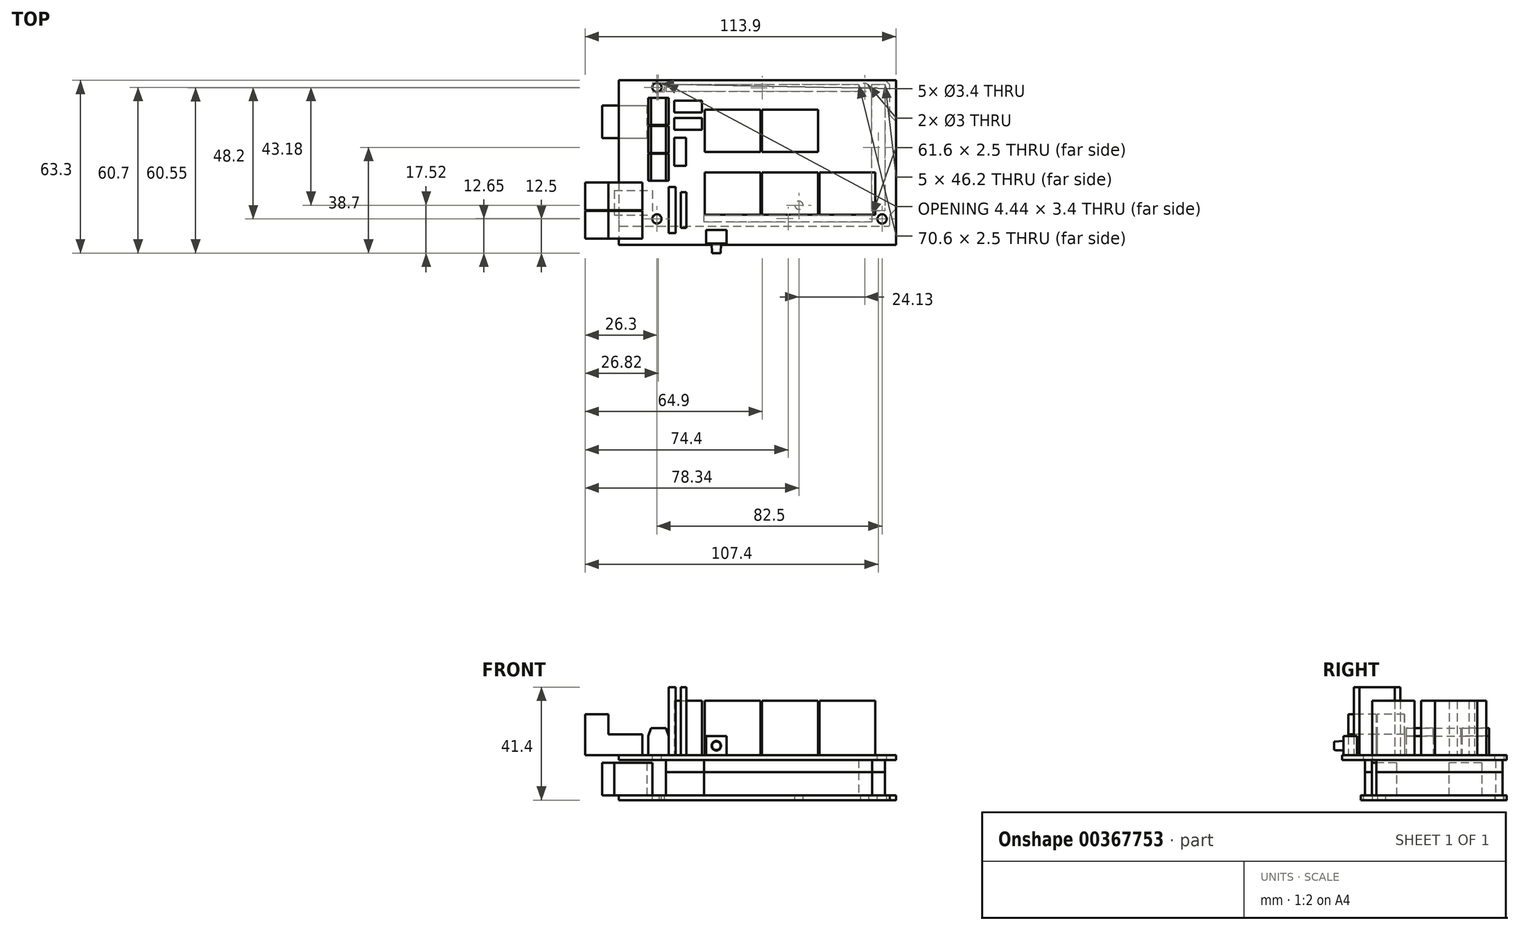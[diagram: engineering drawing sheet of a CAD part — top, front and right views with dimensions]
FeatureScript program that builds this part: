
annotation { "Feature Type Name" : "Feature", "Feature Type Description" : "" }
export const myFeature = defineFeature(function(context is Context, id is Id, definition is map)
    precondition{}
    {
        {
            var Q0;
            Q0=qCreatedBy(makeId("Top.planeOp"),FACE);
            var sketch = newSketch(context, id + "F0", { "sketchPlane" : qUnion([Q0])});
            skLineSegment(sketch, "E0.bottom", {"start": v(-50.8, 26.7) * mm, "end": v(50.8, 26.7) * mm, "construction": true});
            skLineSegment(sketch, "E0.top", {"start": v(-50.8, -26.7) * mm, "end": v(50.8, -26.7) * mm, "construction": true});
            skLineSegment(sketch, "E0.left", {"start": v(-50.8, 26.7) * mm, "end": v(-50.8, -26.7) * mm});
            skLineSegment(sketch, "E0.right", {"start": v(50.8, 26.7) * mm, "end": v(50.8, -26.7) * mm, "construction": true});
            skLineSegment(sketch, "E1", {"start": v(50.8, -26.7) * mm, "end": v(-50.8, 26.7) * mm, "construction": true});
            skLineSegment(sketch, "E2", {"start": v(-50.8, -26.7) * mm, "end": v(48.5, -26.7) * mm});
            skLineSegment(sketch, "E3", {"start": v(48.5, -26.7) * mm, "end": v(48.5, -22.7) * mm});
            skLineSegment(sketch, "E4", {"start": v(48.5, -22.7) * mm, "end": v(50.8, -20.4) * mm});
            skLineSegment(sketch, "E5", {"start": v(50.8, -20.4) * mm, "end": v(50.8, 11.6) * mm});
            skLineSegment(sketch, "E6", {"start": v(50.8, 11.6) * mm, "end": v(48.5, 13.9) * mm});
            skLineSegment(sketch, "E7", {"start": v(48.5, 13.9) * mm, "end": v(48.5, 25.1) * mm});
            skLineSegment(sketch, "E8", {"start": v(48.5, 25.1) * mm, "end": v(46.9, 26.7) * mm});
            skLineSegment(sketch, "E9", {"start": v(46.9, 26.7) * mm, "end": v(-50.8, 26.7) * mm});
            skSolve(sketch);
        }
        {
            var Q0;
            Q0=makeQuery(id+"F0.imprint","IMPRINT",FACE,{"disambiguationData":[TD([[makeQuery(id+"F0.imprint","IMPRINT",EDGE,{"derivedFrom":sQuery(id+"F0.wireOp",EDGE,"E0.left")}),1.0]])]});
            extrude(context, id + "F1", {"entities" : qUnion([Q0]), "depth" : 1.7 * mm});
        }
        {
            var Q0;
            Q0=makeQuery(id+"F1.opExtrude","CAP_FACE",FACE,{"disambiguationData":[OSD([sQuery(id+"F0.wireOp",EDGE,"E0.left"),sQuery(id+"F0.wireOp",EDGE,"E2"),sQuery(id+"F0.wireOp",EDGE,"E3"),sQuery(id+"F0.wireOp",EDGE,"E4"),sQuery(id+"F0.wireOp",EDGE,"E5"),sQuery(id+"F0.wireOp",EDGE,"E6"),sQuery(id+"F0.wireOp",EDGE,"E7"),sQuery(id+"F0.wireOp",EDGE,"E8"),sQuery(id+"F0.wireOp",EDGE,"E9")])],"isStart":false});
            var sketch = newSketch(context, id + "F2", { "sketchPlane" : qUnion([Q0])});
            skPoint(sketch, "E10", {"position": v(-35.56, 24.1) * mm});
            skPoint(sketch, "E11", {"position": v(39.37, 24.1) * mm});
            skPoint(sketch, "E12", {"position": v(15.24, -19.08) * mm});
            skPoint(sketch, "E13", {"position": v(-36.83, -24.16) * mm});
            skPoint(sketch, "E14", {"position": v(45.72, -24.16) * mm});
            skSolve(sketch);
        }
        {
            var Q0;
            Q0=sQuery(id+"F2.wireOp",VERTEX,"E10");
            var Q1;
            Q1=sQuery(id+"F2.wireOp",VERTEX,"E11");
            var Q2;
            Q2=sQuery(id+"F2.wireOp",VERTEX,"E12");
            var Q3;
            Q3=sQuery(id+"F2.wireOp",VERTEX,"E14");
            var Q4;
            Q4=sQuery(id+"F2.wireOp",VERTEX,"E13");
            var Q5;
            Q5=makeQuery(id+"F1.opExtrude","SWEPT_BODY",BODY,{"disambiguationData":[OSD([sQuery(id+"F0.wireOp",EDGE,"E0.left"),sQuery(id+"F0.wireOp",EDGE,"E2"),sQuery(id+"F0.wireOp",EDGE,"E3"),sQuery(id+"F0.wireOp",EDGE,"E4"),sQuery(id+"F0.wireOp",EDGE,"E5"),sQuery(id+"F0.wireOp",EDGE,"E6"),sQuery(id+"F0.wireOp",EDGE,"E7"),sQuery(id+"F0.wireOp",EDGE,"E8"),sQuery(id+"F0.wireOp",EDGE,"E9")])]});
            hole(context, id + "F3", {"style" : HoleStyle.SIMPLE, "endStyle" : HoleEndStyle.THROUGH, "holeDiameter" : 3 * mm, "locations" : qUnion([Q0, Q1, Q2, Q3, Q4]), "scope" : qUnion([Q5]), "isTappedThrough" : true});
        }
        {
            var Q0;
            Q0=makeQuery(id+"F1.opExtrude","SWEPT_EDGE",EDGE,{"disambiguationData":[OSD([sQuery(id+"F0.wireOp",EDGE,"E0.left"),sQuery(id+"F0.wireOp",EDGE,"E9")])]});
            var Q1;
            Q1=makeQuery(id+"F1.opExtrude","SWEPT_EDGE",EDGE,{"disambiguationData":[OSD([sQuery(id+"F0.wireOp",EDGE,"E0.left"),sQuery(id+"F0.wireOp",EDGE,"E2")])]});
            var Q2;
            Q2=makeQuery(id+"F1.opExtrude","SWEPT_EDGE",EDGE,{"disambiguationData":[OSD([sQuery(id+"F0.wireOp",EDGE,"E2"),sQuery(id+"F0.wireOp",EDGE,"E3")])]});
            var Q3;
            Q3=makeQuery(id+"F1.opExtrude","SWEPT_EDGE",EDGE,{"disambiguationData":[OSD([sQuery(id+"F0.wireOp",EDGE,"E3"),sQuery(id+"F0.wireOp",EDGE,"E4")])]});
            var Q4;
            Q4=makeQuery(id+"F1.opExtrude","SWEPT_EDGE",EDGE,{"disambiguationData":[OSD([sQuery(id+"F0.wireOp",EDGE,"E4"),sQuery(id+"F0.wireOp",EDGE,"E5")])]});
            var Q5;
            Q5=makeQuery(id+"F1.opExtrude","SWEPT_EDGE",EDGE,{"disambiguationData":[OSD([sQuery(id+"F0.wireOp",EDGE,"E5"),sQuery(id+"F0.wireOp",EDGE,"E6")])]});
            var Q6;
            Q6=makeQuery(id+"F1.opExtrude","SWEPT_EDGE",EDGE,{"disambiguationData":[OSD([sQuery(id+"F0.wireOp",EDGE,"E6"),sQuery(id+"F0.wireOp",EDGE,"E7")])]});
            var Q7;
            Q7=makeQuery(id+"F1.opExtrude","SWEPT_EDGE",EDGE,{"disambiguationData":[OSD([sQuery(id+"F0.wireOp",EDGE,"E7"),sQuery(id+"F0.wireOp",EDGE,"E8")])]});
            var Q8;
            Q8=makeQuery(id+"F1.opExtrude","SWEPT_EDGE",EDGE,{"disambiguationData":[OSD([sQuery(id+"F0.wireOp",EDGE,"E8"),sQuery(id+"F0.wireOp",EDGE,"E9")])]});
            fillet(context, id + "F4", {"entities" : qUnion([Q0, Q1, Q2, Q3, Q4, Q5, Q6, Q7, Q8]), "radius" : .5 * mm, "tangentPropagation" : true, "allowEdgeOverflow" : false});
        }
        {
            var Q0;
            Q0=makeQuery(id+"F1.opExtrude","CAP_FACE",FACE,{"disambiguationData":[OSD([sQuery(id+"F0.wireOp",EDGE,"E0.left"),sQuery(id+"F0.wireOp",EDGE,"E2"),sQuery(id+"F0.wireOp",EDGE,"E3"),sQuery(id+"F0.wireOp",EDGE,"E4"),sQuery(id+"F0.wireOp",EDGE,"E5"),sQuery(id+"F0.wireOp",EDGE,"E6"),sQuery(id+"F0.wireOp",EDGE,"E7"),sQuery(id+"F0.wireOp",EDGE,"E8"),sQuery(id+"F0.wireOp",EDGE,"E9")])],"isStart":false});
            var sketch = newSketch(context, id + "F5", { "sketchPlane" : qUnion([Q0])});
            skLineSegment(sketch, "E15.bottom", {"start": v(-52.4, -13.7) * mm, "end": v(-38.4, -13.7) * mm});
            skLineSegment(sketch, "E15.top", {"start": v(-52.4, -22.7) * mm, "end": v(-38.4, -22.7) * mm});
            skLineSegment(sketch, "E15.left", {"start": v(-52.4, -13.7) * mm, "end": v(-52.4, -22.7) * mm});
            skLineSegment(sketch, "E15.right", {"start": v(-38.4, -13.7) * mm, "end": v(-38.4, -22.7) * mm});
            skLineSegment(sketch, "E16.bottom", {"start": v(-56.9, 17.5) * mm, "end": v(-40.5, 17.5) * mm});
            skLineSegment(sketch, "E16.top", {"start": v(-56.9, 5.5) * mm, "end": v(-40.5, 5.5) * mm});
            skLineSegment(sketch, "E16.left", {"start": v(-56.9, 17.5) * mm, "end": v(-56.9, 5.5) * mm});
            skLineSegment(sketch, "E16.right", {"start": v(-40.5, 17.5) * mm, "end": v(-40.5, 5.5) * mm});
            skSolve(sketch);
        }
        {
            var Q0;
            {var subQ0=sQuery(id+"F5.wireOp",EDGE,"E16.left");Q0=makeQuery(id+"F5.imprint","IMPRINT",FACE,{"disambiguationData":[TD([[makeQuery(id+"F5.imprint","IMPRINT",EDGE,{"derivedFrom":subQ0}),1.0]])]});}
            var Q1;
            {var subQ0=sQuery(id+"F5.wireOp",EDGE,"E16.right");Q1=makeQuery(id+"F5.imprint","IMPRINT",FACE,{"disambiguationData":[TD([[makeQuery(id+"F5.imprint","IMPRINT",EDGE,{"derivedFrom":subQ0}),-1.0]])]});}
            var Q2;
            {var subQ0=sQuery(id+"F5.wireOp",EDGE,"E15.right");Q2=makeQuery(id+"F5.imprint","IMPRINT",FACE,{"disambiguationData":[TD([[makeQuery(id+"F5.imprint","IMPRINT",EDGE,{"derivedFrom":subQ0}),-1.0]])]});}
            var Q3;
            {var subQ0=sQuery(id+"F5.wireOp",EDGE,"E15.left");Q3=makeQuery(id+"F5.imprint","IMPRINT",FACE,{"disambiguationData":[TD([[makeQuery(id+"F5.imprint","IMPRINT",EDGE,{"derivedFrom":subQ0}),1.0]])]});}
            extrude(context, id + "F6", {"entities" : qUnion([Q0, Q1, Q2, Q3]), "depth" : 12 * mm});
        }
        {
            var Q0;
            Q0=makeQuery(id+"F1.opExtrude","CAP_FACE",FACE,{"disambiguationData":[OSD([sQuery(id+"F0.wireOp",EDGE,"E0.left"),sQuery(id+"F0.wireOp",EDGE,"E2"),sQuery(id+"F0.wireOp",EDGE,"E3"),sQuery(id+"F0.wireOp",EDGE,"E4"),sQuery(id+"F0.wireOp",EDGE,"E5"),sQuery(id+"F0.wireOp",EDGE,"E6"),sQuery(id+"F0.wireOp",EDGE,"E7"),sQuery(id+"F0.wireOp",EDGE,"E8"),sQuery(id+"F0.wireOp",EDGE,"E9")])],"isStart":false});
            var sketch = newSketch(context, id + "F7", { "sketchPlane" : qUnion([Q0])});
            skLineSegment(sketch, "E17.bottom", {"start": v(-33.5, 25.2) * mm, "end": v(37.1, 25.2) * mm});
            skLineSegment(sketch, "E17.top", {"start": v(-33.5, 22.7) * mm, "end": v(37.1, 22.7) * mm});
            skLineSegment(sketch, "E17.left", {"start": v(-33.5, 25.2) * mm, "end": v(-33.5, 22.7) * mm});
            skLineSegment(sketch, "E17.right", {"start": v(37.1, 25.2) * mm, "end": v(37.1, 22.7) * mm});
            skLineSegment(sketch, "E18.bottom", {"start": v(41.8, 25.2) * mm, "end": v(46.8, 25.2) * mm});
            skLineSegment(sketch, "E18.top", {"start": v(41.8, -21) * mm, "end": v(46.8, -21) * mm});
            skLineSegment(sketch, "E18.left", {"start": v(41.8, 25.2) * mm, "end": v(41.8, -21) * mm});
            skLineSegment(sketch, "E18.right", {"start": v(46.8, 25.2) * mm, "end": v(46.8, -21) * mm});
            skLineSegment(sketch, "E19.bottom", {"start": v(42.1, -25.2) * mm, "end": v(-19.5, -25.2) * mm});
            skLineSegment(sketch, "E19.top", {"start": v(42.1, -22.7) * mm, "end": v(-19.5, -22.7) * mm});
            skLineSegment(sketch, "E19.left", {"start": v(42.1, -25.2) * mm, "end": v(42.1, -22.7) * mm});
            skLineSegment(sketch, "E19.right", {"start": v(-19.5, -25.2) * mm, "end": v(-19.5, -22.7) * mm});
            skSolve(sketch);
        }
        {
            var Q0;
            Q0=qSketchRegion(id+"F7",true);
            extrude(context, id + "F8", {"entities" : qUnion([Q0]), "operationType" : NewBodyOperationType.ADD, "depth" : 8.6 * mm});
        }
        {
            var Q0;
            Q0=makeQuery(id+"F8.opExtrude","CAP_FACE",FACE,{"disambiguationData":[OSD([sQuery(id+"F7.wireOp",EDGE,"E17.bottom"),sQuery(id+"F7.wireOp",EDGE,"E17.top"),sQuery(id+"F7.wireOp",EDGE,"E17.left"),sQuery(id+"F7.wireOp",EDGE,"E17.right")])],"isStart":false});
            var sketch = newSketch(context, id + "F9", { "sketchPlane" : qUnion([Q0])});
            skLineSegment(sketch, "E20.1.0", {"start": v(41.8, 25.2) * mm, "end": v(41.8, -21) * mm});
            skLineSegment(sketch, "E20.1.1", {"start": v(41.8, -21) * mm, "end": v(46.8, -21) * mm});
            skLineSegment(sketch, "E20.1.2", {"start": v(46.8, -21) * mm, "end": v(46.8, 25.2) * mm});
            skLineSegment(sketch, "E20.1.3", {"start": v(46.8, 25.2) * mm, "end": v(41.8, 25.2) * mm});
            skLineSegment(sketch, "E20.2.0", {"start": v(42.1, -25.2) * mm, "end": v(42.1, -22.7) * mm});
            skLineSegment(sketch, "E20.2.1", {"start": v(42.1, -22.7) * mm, "end": v(-19.5, -22.7) * mm});
            skLineSegment(sketch, "E20.2.2", {"start": v(-19.5, -22.7) * mm, "end": v(-19.5, -25.2) * mm});
            skLineSegment(sketch, "E20.2.3", {"start": v(-19.5, -25.2) * mm, "end": v(42.1, -25.2) * mm});
            skLineSegment(sketch, "E21.0", {"start": v(-33.5, 22.7) * mm, "end": v(37.1, 22.7) * mm});
            skLineSegment(sketch, "E22.0", {"start": v(-33.5, 25.2) * mm, "end": v(-33.5, 22.7) * mm});
            skLineSegment(sketch, "E22.1", {"start": v(-33.5, 25.2) * mm, "end": v(37.1, 25.2) * mm});
            skLineSegment(sketch, "E22.2", {"start": v(37.1, 25.2) * mm, "end": v(37.1, 22.7) * mm});
            skSolve(sketch);
        }
        {
            var Q0;
            Q0=qSketchRegion(id+"F9",true);
            extrude(context, id + "F10", {"entities" : qUnion([Q0]), "depth" : 4.4 * mm});
        }
        {
            var Q0;
            Q0=makeQuery(id+"F10.opExtrude","CAP_FACE",FACE,{"disambiguationData":[OSD([sQuery(id+"F9.wireOp",EDGE,"E21.0"),sQuery(id+"F9.wireOp",EDGE,"E22.0"),sQuery(id+"F9.wireOp",EDGE,"E22.1"),sQuery(id+"F9.wireOp",EDGE,"E22.2")])],"isStart":false});
            var sketch = newSketch(context, id + "F11", { "sketchPlane" : qUnion([Q0])});
            skLineSegment(sketch, "E23", {"start": v(50.8, 26.7) * mm, "end": v(-50.8, 26.7) * mm});
            skLineSegment(sketch, "E24", {"start": v(-50.8, 26.7) * mm, "end": v(-50.8, -33.6) * mm});
            skLineSegment(sketch, "E25", {"start": v(-50.8, -33.6) * mm, "end": v(50.8, -33.6) * mm});
            skLineSegment(sketch, "E26", {"start": v(50.8, -33.6) * mm, "end": v(50.8, 26.7) * mm});
            skSolve(sketch);
        }
        {
            var Q0;
            Q0=qSketchRegion(id+"F11",true);
            extrude(context, id + "F12", {"entities" : qUnion([Q0]), "operationType" : NewBodyOperationType.ADD, "depth" : 1.7 * mm});
        }
        {
            var Q0;
            Q0=makeQuery(id+"F12.opExtrude","CAP_FACE",FACE,{"disambiguationData":[OSD([sQuery(id+"F11.wireOp",EDGE,"E23"),sQuery(id+"F11.wireOp",EDGE,"E24"),sQuery(id+"F11.wireOp",EDGE,"E25"),sQuery(id+"F11.wireOp",EDGE,"E26")])],"isStart":false});
            var sketch = newSketch(context, id + "F13", { "sketchPlane" : qUnion([Q0])});
            skPoint(sketch, "E27", {"position": v(-36.8, 24.1) * mm});
            skPoint(sketch, "E28", {"position": v(-36.8, -24.1) * mm});
            skPoint(sketch, "E29", {"position": v(45.7, -24.1) * mm});
            skSolve(sketch);
        }
        {
            var Q0;
            Q0=sQuery(id+"F13.wireOp",VERTEX,"E28");
            var Q1;
            Q1=sQuery(id+"F13.wireOp",VERTEX,"E27");
            var Q2;
            Q2=sQuery(id+"F13.wireOp",VERTEX,"E29");
            var Q3;
            Q3=makeQuery(id+"F1.opExtrude","SWEPT_BODY",BODY,{"disambiguationData":[OSD([sQuery(id+"F0.wireOp",EDGE,"E0.left"),sQuery(id+"F0.wireOp",EDGE,"E2"),sQuery(id+"F0.wireOp",EDGE,"E3"),sQuery(id+"F0.wireOp",EDGE,"E4"),sQuery(id+"F0.wireOp",EDGE,"E5"),sQuery(id+"F0.wireOp",EDGE,"E6"),sQuery(id+"F0.wireOp",EDGE,"E7"),sQuery(id+"F0.wireOp",EDGE,"E8"),sQuery(id+"F0.wireOp",EDGE,"E9")])]});
            var Q4;
            Q4=makeQuery(id+"F10.opExtrude","SWEPT_BODY",BODY,{"disambiguationData":[OSD([sQuery(id+"F9.wireOp",EDGE,"E20.1.0"),sQuery(id+"F9.wireOp",EDGE,"E20.1.1"),sQuery(id+"F9.wireOp",EDGE,"E20.1.2"),sQuery(id+"F9.wireOp",EDGE,"E20.1.3")])]});
            hole(context, id + "F14", {"style" : HoleStyle.SIMPLE, "endStyle" : HoleEndStyle.THROUGH, "holeDiameter" : 3.4 * mm, "locations" : qUnion([Q0, Q1, Q2]), "scope" : qUnion([Q3, Q4]), "isTappedThrough" : true});
        }
        {
            var Q0;
            Q0=makeQuery(id+"F12.opExtrude","CAP_FACE",FACE,{"disambiguationData":[OSD([sQuery(id+"F11.wireOp",EDGE,"E23"),sQuery(id+"F11.wireOp",EDGE,"E24"),sQuery(id+"F11.wireOp",EDGE,"E25"),sQuery(id+"F11.wireOp",EDGE,"E26")])],"isStart":false});
            var sketch = newSketch(context, id + "F15", { "sketchPlane" : qUnion([Q0])});
            skLineSegment(sketch, "E30.bottom", {"start": v(-42.1, -21.15) * mm, "end": v(-63.1, -21.15) * mm});
            skLineSegment(sketch, "E30.top", {"start": v(-42.1, -31.3) * mm, "end": v(-63.1, -31.3) * mm});
            skLineSegment(sketch, "E30.left", {"start": v(-42.1, -21.15) * mm, "end": v(-42.1, -31.3) * mm});
            skLineSegment(sketch, "E30.right", {"start": v(-63.1, -21.15) * mm, "end": v(-63.1, -31.3) * mm});
            skLineSegment(sketch, "E31.bottom", {"start": v(-42.1, -10.7) * mm, "end": v(-63.1, -10.7) * mm});
            skLineSegment(sketch, "E31.top", {"start": v(-42.1, -20.85) * mm, "end": v(-63.1, -20.85) * mm});
            skLineSegment(sketch, "E31.left", {"start": v(-42.1, -10.7) * mm, "end": v(-42.1, -20.85) * mm});
            skLineSegment(sketch, "E31.right", {"start": v(-63.1, -10.7) * mm, "end": v(-63.1, -20.85) * mm});
            skSolve(sketch);
        }
        {
            var Q0;
            Q0=qSketchRegion(id+"F15",true);
            extrude(context, id + "F16", {"entities" : qUnion([Q0]), "depth" : 15 * mm});
        }
        {
            var Q0;
            Q0=makeQuery(id+"F16.opExtrude","SWEPT_FACE",FACE,{"disambiguationData":[OSD([sQuery(id+"F15.wireOp",EDGE,"E30.top")])]});
            var sketch = newSketch(context, id + "F17", { "sketchPlane" : qUnion([Q0])});
            skLineSegment(sketch, "E32.bottom", {"start": v(-54.6, 31.4) * mm, "end": v(-42.1, 31.4) * mm});
            skLineSegment(sketch, "E32.top", {"start": v(-54.6, 24.1) * mm, "end": v(-42.1, 24.1) * mm});
            skLineSegment(sketch, "E32.left", {"start": v(-54.6, 31.4) * mm, "end": v(-54.6, 24.1) * mm});
            skLineSegment(sketch, "E32.right", {"start": v(-42.1, 31.4) * mm, "end": v(-42.1, 24.1) * mm});
            skSolve(sketch);
        }
        {
            var Q0;
            Q0=qSketchRegion(id+"F17",true);
            var Q1;
            Q1=makeQuery(id+"F16.opExtrude","SWEPT_FACE",FACE,{"disambiguationData":[OSD([sQuery(id+"F15.wireOp",EDGE,"E31.bottom")])]});
            extrude(context, id + "F18", {"entities" : qUnion([Q0]), "operationType" : NewBodyOperationType.REMOVE, "endBound" : BoundingType.UP_TO_SURFACE, "oppositeDirection" : true, "endBoundEntityFace" : qUnion([Q1]), "depth" : 25 * mm});
        }
        {
            var Q0;
            Q0=makeQuery(id+"F12.opExtrude","CAP_FACE",FACE,{"disambiguationData":[OSD([sQuery(id+"F11.wireOp",EDGE,"E23"),sQuery(id+"F11.wireOp",EDGE,"E24"),sQuery(id+"F11.wireOp",EDGE,"E25"),sQuery(id+"F11.wireOp",EDGE,"E26")])],"isStart":false});
            var sketch = newSketch(context, id + "F19", { "sketchPlane" : qUnion([Q0])});
            skLineSegment(sketch, "E33.bottom", {"start": v(-40, 20.2) * mm, "end": v(-32.5, 20.2) * mm});
            skLineSegment(sketch, "E33.top", {"start": v(-40, 10.3) * mm, "end": v(-32.5, 10.3) * mm});
            skLineSegment(sketch, "E33.left", {"start": v(-40, 20.2) * mm, "end": v(-40, 10.3) * mm});
            skLineSegment(sketch, "E33.right", {"start": v(-32.5, 20.2) * mm, "end": v(-32.5, 10.3) * mm});
            skLineSegment(sketch, "E34.bottom", {"start": v(-40, 10) * mm, "end": v(-32.5, 10) * mm});
            skLineSegment(sketch, "E34.top", {"start": v(-40, 0.1) * mm, "end": v(-32.5, 0.1) * mm});
            skLineSegment(sketch, "E34.left", {"start": v(-40, 10) * mm, "end": v(-40, 0.1) * mm});
            skLineSegment(sketch, "E34.right", {"start": v(-32.5, 10) * mm, "end": v(-32.5, 0.1) * mm});
            skLineSegment(sketch, "E35.bottom", {"start": v(-40, -0.2) * mm, "end": v(-32.5, -0.2) * mm});
            skLineSegment(sketch, "E35.top", {"start": v(-40, -10.1) * mm, "end": v(-32.5, -10.1) * mm});
            skLineSegment(sketch, "E35.left", {"start": v(-40, -0.2) * mm, "end": v(-40, -10.1) * mm});
            skLineSegment(sketch, "E35.right", {"start": v(-32.5, -0.2) * mm, "end": v(-32.5, -10.1) * mm});
            skSolve(sketch);
        }
        {
            var Q0;
            Q0=qSketchRegion(id+"F19",true);
            extrude(context, id + "F20", {"entities" : qUnion([Q0]), "depth" : 10 * mm});
        }
        {
            var Q0;
            Q0=makeQuery(id+"F20.opExtrude","CAP_EDGE",EDGE,{"disambiguationData":[OSD([sQuery(id+"F19.wireOp",EDGE,"E33.left")])],"isStart":false});
            var Q1;
            Q1=makeQuery(id+"F20.opExtrude","CAP_EDGE",EDGE,{"disambiguationData":[OSD([sQuery(id+"F19.wireOp",EDGE,"E34.left")])],"isStart":false});
            var Q2;
            Q2=makeQuery(id+"F20.opExtrude","CAP_EDGE",EDGE,{"disambiguationData":[OSD([sQuery(id+"F19.wireOp",EDGE,"E35.left")])],"isStart":false});
            var Q3;
            Q3=makeQuery(id+"F20.opExtrude","CAP_EDGE",EDGE,{"disambiguationData":[OSD([sQuery(id+"F19.wireOp",EDGE,"E35.right")])],"isStart":false});
            var Q4;
            Q4=makeQuery(id+"F20.opExtrude","CAP_EDGE",EDGE,{"disambiguationData":[OSD([sQuery(id+"F19.wireOp",EDGE,"E34.right")])],"isStart":false});
            var Q5;
            Q5=makeQuery(id+"F20.opExtrude","CAP_EDGE",EDGE,{"disambiguationData":[OSD([sQuery(id+"F19.wireOp",EDGE,"E33.right")])],"isStart":false});
            chamfer(context, id + "F21", {"entities" : qUnion([Q0, Q1, Q2, Q3, Q4, Q5]), "chamferType" : ChamferType.TWO_OFFSETS, "width1" : 1 * mm, "oppositeDirection" : false, "width2" : 3 * mm, "tangentPropagation" : true});
        }
        {
            var Q0;
            Q0=makeQuery(id+"F12.opExtrude","CAP_FACE",FACE,{"disambiguationData":[OSD([sQuery(id+"F11.wireOp",EDGE,"E23"),sQuery(id+"F11.wireOp",EDGE,"E24"),sQuery(id+"F11.wireOp",EDGE,"E25"),sQuery(id+"F11.wireOp",EDGE,"E26")])],"isStart":false});
            var sketch = newSketch(context, id + "F22", { "sketchPlane" : qUnion([Q0])});
            skLineSegment(sketch, "E36.bottom", {"start": v(-30.5, 19.2) * mm, "end": v(-20.3, 19.2) * mm});
            skLineSegment(sketch, "E36.top", {"start": v(-30.5, 14.9) * mm, "end": v(-20.3, 14.9) * mm});
            skLineSegment(sketch, "E36.left", {"start": v(-30.5, 19.2) * mm, "end": v(-30.5, 14.9) * mm});
            skLineSegment(sketch, "E36.right", {"start": v(-20.3, 19.2) * mm, "end": v(-20.3, 14.9) * mm});
            skLineSegment(sketch, "E37.bottom", {"start": v(-30.5, 12.9) * mm, "end": v(-20.3, 12.9) * mm});
            skLineSegment(sketch, "E37.top", {"start": v(-30.5, 8.6) * mm, "end": v(-20.3, 8.6) * mm});
            skLineSegment(sketch, "E37.left", {"start": v(-30.5, 12.9) * mm, "end": v(-30.5, 8.6) * mm});
            skLineSegment(sketch, "E37.right", {"start": v(-20.3, 12.9) * mm, "end": v(-20.3, 8.6) * mm});
            skLineSegment(sketch, "E38.bottom", {"start": v(-30.5, 5.6) * mm, "end": v(-26.2, 5.6) * mm});
            skLineSegment(sketch, "E38.top", {"start": v(-30.5, -4.6) * mm, "end": v(-26.2, -4.6) * mm});
            skLineSegment(sketch, "E38.left", {"start": v(-30.5, 5.6) * mm, "end": v(-30.5, -4.6) * mm});
            skLineSegment(sketch, "E38.right", {"start": v(-26.2, 5.6) * mm, "end": v(-26.2, -4.6) * mm});
            skLineSegment(sketch, "E39.bottom", {"start": v(-19.3, 15.9) * mm, "end": v(1.2, 15.9) * mm});
            skLineSegment(sketch, "E39.top", {"start": v(-19.3, 0.4) * mm, "end": v(1.2, 0.4) * mm});
            skLineSegment(sketch, "E39.left", {"start": v(-19.3, 15.9) * mm, "end": v(-19.3, 0.4) * mm});
            skLineSegment(sketch, "E39.right", {"start": v(1.2, 15.9) * mm, "end": v(1.2, 0.4) * mm});
            skLineSegment(sketch, "E40.bottom", {"start": v(1.7, 15.9) * mm, "end": v(22.2, 15.9) * mm});
            skLineSegment(sketch, "E40.top", {"start": v(1.7, 0.4) * mm, "end": v(22.2, 0.4) * mm});
            skLineSegment(sketch, "E40.left", {"start": v(1.7, 15.9) * mm, "end": v(1.7, 0.4) * mm});
            skLineSegment(sketch, "E40.right", {"start": v(22.2, 15.9) * mm, "end": v(22.2, 0.4) * mm});
            skLineSegment(sketch, "E41.bottom", {"start": v(-19.3, -7.1) * mm, "end": v(1.2, -7.1) * mm});
            skLineSegment(sketch, "E41.top", {"start": v(-19.3, -22.6) * mm, "end": v(1.2, -22.6) * mm});
            skLineSegment(sketch, "E41.left", {"start": v(-19.3, -7.1) * mm, "end": v(-19.3, -22.6) * mm});
            skLineSegment(sketch, "E41.right", {"start": v(1.2, -7.1) * mm, "end": v(1.2, -22.6) * mm});
            skLineSegment(sketch, "E42.bottom", {"start": v(1.7, -7.1) * mm, "end": v(22.2, -7.1) * mm});
            skLineSegment(sketch, "E42.top", {"start": v(1.7, -22.6) * mm, "end": v(22.2, -22.6) * mm});
            skLineSegment(sketch, "E42.left", {"start": v(1.7, -7.1) * mm, "end": v(1.7, -22.6) * mm});
            skLineSegment(sketch, "E42.right", {"start": v(22.2, -7.1) * mm, "end": v(22.2, -22.6) * mm});
            skLineSegment(sketch, "E43.bottom", {"start": v(22.7, -7.1) * mm, "end": v(43.2, -7.1) * mm});
            skLineSegment(sketch, "E43.top", {"start": v(22.7, -22.6) * mm, "end": v(43.2, -22.6) * mm});
            skLineSegment(sketch, "E43.left", {"start": v(22.7, -7.1) * mm, "end": v(22.7, -22.6) * mm});
            skLineSegment(sketch, "E43.right", {"start": v(43.2, -7.1) * mm, "end": v(43.2, -22.6) * mm});
            skSolve(sketch);
        }
        {
            var Q0;
            Q0=qSketchRegion(id+"F22",true);
            extrude(context, id + "F23", {"entities" : qUnion([Q0]), "operationType" : NewBodyOperationType.ADD, "depth" : 20 * mm});
        }
        {
            var Q0;
            Q0=makeQuery(id+"F12.opExtrude","CAP_FACE",FACE,{"disambiguationData":[OSD([sQuery(id+"F11.wireOp",EDGE,"E23"),sQuery(id+"F11.wireOp",EDGE,"E24"),sQuery(id+"F11.wireOp",EDGE,"E25"),sQuery(id+"F11.wireOp",EDGE,"E26")])],"isStart":false});
            var sketch = newSketch(context, id + "F24", { "sketchPlane" : qUnion([Q0])});
            skLineSegment(sketch, "E44.bottom", {"start": v(-32.5, -12.33) * mm, "end": v(-30, -12.33) * mm});
            skLineSegment(sketch, "E44.top", {"start": v(-32.5, -29.33) * mm, "end": v(-30, -29.33) * mm});
            skLineSegment(sketch, "E44.left", {"start": v(-32.5, -12.33) * mm, "end": v(-32.5, -29.33) * mm});
            skLineSegment(sketch, "E44.right", {"start": v(-30, -12.33) * mm, "end": v(-30, -29.33) * mm});
            skLineSegment(sketch, "E45.bottom", {"start": v(-28, -14.33) * mm, "end": v(-26, -14.33) * mm});
            skLineSegment(sketch, "E45.top", {"start": v(-28, -27.33) * mm, "end": v(-26, -27.33) * mm});
            skLineSegment(sketch, "E45.left", {"start": v(-28, -14.33) * mm, "end": v(-28, -27.33) * mm});
            skLineSegment(sketch, "E45.right", {"start": v(-26, -14.33) * mm, "end": v(-26, -27.33) * mm});
            skLineSegment(sketch, "E46", {"start": v(-30, -20.83) * mm, "end": v(-28, -20.83) * mm});
            skSolve(sketch);
        }
        {
            var Q0;
            Q0=qSketchRegion(id+"F24",true);
            extrude(context, id + "F25", {"entities" : qUnion([Q0]), "depth" : 25 * mm});
        }
        {
            var Q0;
            Q0=makeQuery(id+"F12.opExtrude","CAP_FACE",FACE,{"disambiguationData":[OSD([sQuery(id+"F11.wireOp",EDGE,"E23"),sQuery(id+"F11.wireOp",EDGE,"E24"),sQuery(id+"F11.wireOp",EDGE,"E25"),sQuery(id+"F11.wireOp",EDGE,"E26")])],"isStart":false});
            var sketch = newSketch(context, id + "F26", { "sketchPlane" : qUnion([Q0])});
            skLineSegment(sketch, "E47.bottom", {"start": v(-18.8, -28.1) * mm, "end": v(-11.3, -28.1) * mm});
            skLineSegment(sketch, "E47.top", {"start": v(-18.8, -33.1) * mm, "end": v(-11.3, -33.1) * mm});
            skLineSegment(sketch, "E47.left", {"start": v(-18.8, -28.1) * mm, "end": v(-18.8, -33.1) * mm});
            skLineSegment(sketch, "E47.right", {"start": v(-11.3, -28.1) * mm, "end": v(-11.3, -33.1) * mm});
            skSolve(sketch);
        }
        {
            var Q0;
            Q0=qSketchRegion(id+"F26",true);
            extrude(context, id + "F27", {"entities" : qUnion([Q0]), "operationType" : NewBodyOperationType.ADD, "depth" : 7 * mm});
        }
        {
            var Q0;
            Q0=makeQuery(id+"F27.opExtrude","SWEPT_FACE",FACE,{"disambiguationData":[OSD([sQuery(id+"F26.wireOp",EDGE,"E47.top")])]});
            var sketch = newSketch(context, id + "F28", { "sketchPlane" : qUnion([Q0])});
            skCircle(sketch, "E48", {"center": v(-15.05, 19.9) * mm, "radius": 1.75 * mm});
            skLineSegment(sketch, "E49", {"start": v(-18.8, 23.4) * mm, "end": v(-11.3, 16.4) * mm, "construction": true});
            skSolve(sketch);
        }
        {
            var Q0;
            Q0=makeQuery(id+"F28.imprint","IMPRINT",FACE,{"disambiguationData":[TD([[makeQuery(id+"F28.imprint","IMPRINT",EDGE,{"derivedFrom":sQuery(id+"F28.wireOp",EDGE,"E48")}),1.0]])]});
            var Q1;
            Q1=sQuery(id+"F28.wireOp",EDGE,"E48");
            extrude(context, id + "F29", {"entities" : qUnion([Q0]), "operationType" : NewBodyOperationType.ADD, "surfaceEntities" : qUnion([Q1]), "depth" : 3.5 * mm, "hasDraft" : true, "draftAngle" : 3 * degree, "draftPullDirection" : true});
        }
    });
